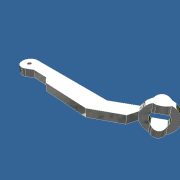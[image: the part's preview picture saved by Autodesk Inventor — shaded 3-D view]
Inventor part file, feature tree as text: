
AUTODESK INVENTOR PART (.ipt)
format: ipt  version: unknown  size: 224,768 bytes
history: native  units: mm
features: extrude x4, sketch x4
ambient origin geometry x8: Origin, YZ Plane, XZ Plane, XY Plane, X Axis, Y Axis, Z Axis, Center Point
feature tree (8):
  extrude  "Выдавливание1"  Depth=1.2mm
  extrude  "Выдавливание2"  Depth=5.0mm
  extrude  "Выдавливание7"  Depth=24.5mm
  extrude  "Выдавливание8"  Depth=5.0mm
  sketch  "Эскиз1"
  sketch  "Эскиз2"
  sketch  "Эскиз3"
  sketch  "Эскиз5"
